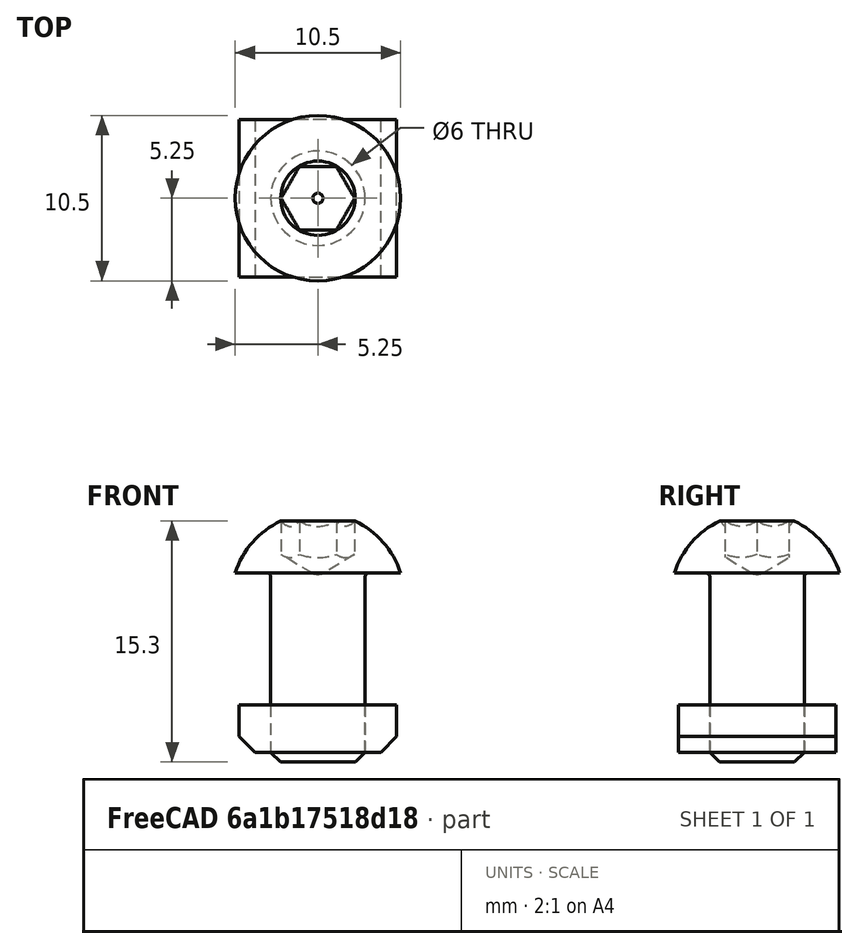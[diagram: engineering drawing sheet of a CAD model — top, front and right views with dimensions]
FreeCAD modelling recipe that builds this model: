
FCSTD DOCUMENT  (FreeCAD 0.17R9796 (Git))
Label: nutplate12screw
License: All rights reserved
LicenseURL: http://en.wikipedia.org/wiki/All_rights_reserved
objects: Part::FeaturePython×1, Part::Feature×1, App::FeaturePython×1, Part::Compound×1
note: 3 computed .brp shape members not serialized (recipe doc carries the construction recipe); baked Part::Feature solids carry a one-line shape summary decoded from their .brp

FEATURE [Part::FeaturePython] Screw  label="M6x12-Screw"  # Fasteners workbench fastener (typed FeaturePython)
  diameter = 4
  invert = false
  length = 1
  matchOuter = false
  offset = 0
  thread = false
  type = 20
FEATURE [Part::Feature] Body001  label="m6nutplate"
  Placement = pos=(5,-5,-8.39) rot=(0,-1,0;3.14159rad)
  shape: bbox 10 x 10 x 3 mm, 9 faces (baked)
FEATURE [App::FeaturePython] circularEdgeConstraint01  # a2plus constraint (typed FeaturePython)
  Object1 = Screw
  Object2 = Body001
  SubElement1 = Edge7
  SubElement2 = Edge20
  Type = circularEdge
  directionConstraint = 1
  lockRotation = false
  offset = 0
FEATURE [Part::Compound] Compound
  Links = -> [Screw,circularEdgeConstraint01,Body001]
